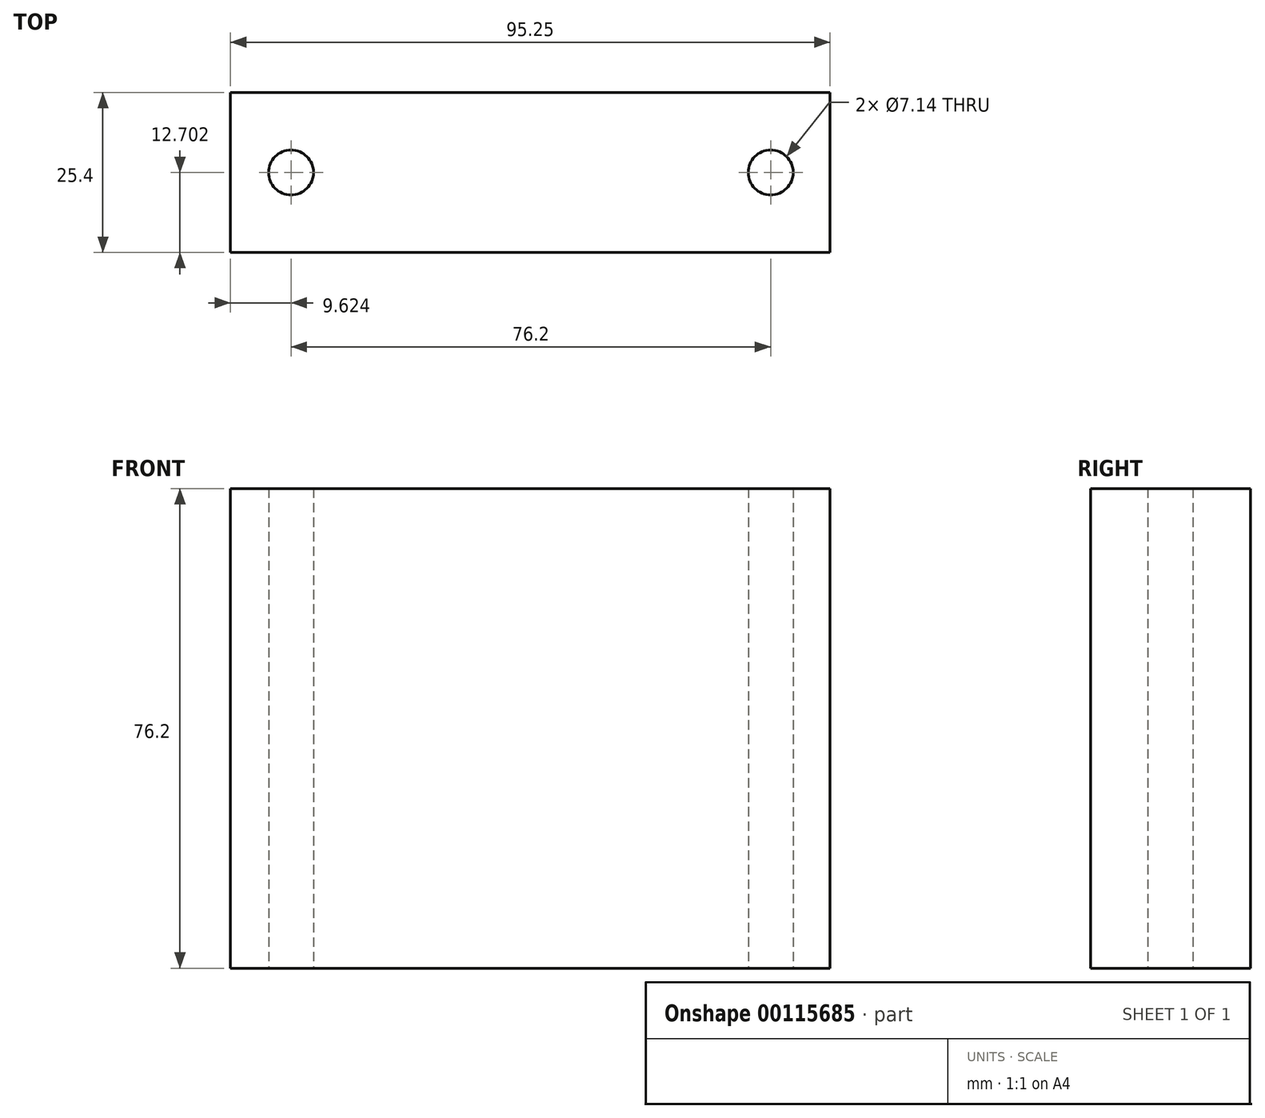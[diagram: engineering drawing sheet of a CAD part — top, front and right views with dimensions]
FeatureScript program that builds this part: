
annotation { "Feature Type Name" : "Feature", "Feature Type Description" : "" }
export const myFeature = defineFeature(function(context is Context, id is Id, definition is map)
    precondition{}
    {
        {
            var Q0;
            Q0=qCreatedBy(makeId("Top.planeOp"),FACE);
            var sketch = newSketch(context, id + "F0", { "sketchPlane" : qUnion([Q0])});
            skLineSegment(sketch, "E0", {"start": v(-47.22, -5.16) * mm, "end": v(48.03, -5.16) * mm});
            skLineSegment(sketch, "E1", {"start": v(48.03, -30.56) * mm, "end": v(48.03, -5.16) * mm});
            skLineSegment(sketch, "E2", {"start": v(48.03, -30.56) * mm, "end": v(-47.22, -30.56) * mm});
            skLineSegment(sketch, "E3", {"start": v(-47.22, -5.16) * mm, "end": v(-47.22, -30.56) * mm});
            skCircle(sketch, "E4", {"center": v(-37.6, -17.86) * mm, "radius": 3.57 * mm});
            skCircle(sketch, "E5", {"center": v(38.6, -17.86) * mm, "radius": 3.57 * mm});
            skLineSegment(sketch, "E6", {"start": v(-37.6, -17.86) * mm, "end": v(38.6, -17.86) * mm, "construction": true});
            skLineSegment(sketch, "E7", {"start": v(-37.6, -17.86) * mm, "end": v(-37.6, -30.56) * mm, "construction": true});
            skLineSegment(sketch, "E8", {"start": v(38.6, -17.86) * mm, "end": v(38.6, -30.56) * mm, "construction": true});
            skSolve(sketch);
        }
        {
            var Q0;
            Q0=makeQuery(id+"F0.imprint","IMPRINT",FACE,{"disambiguationData":[TD([[makeQuery(id+"F0.imprint","IMPRINT",EDGE,{"derivedFrom":sQuery(id+"F0.wireOp",EDGE,"E0")}),-1.0]])]});
            extrude(context, id + "F1", {"entities" : qUnion([Q0]), "depth" : 76.2 * mm});
        }
    });
